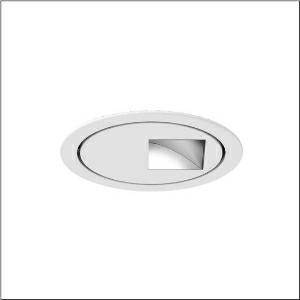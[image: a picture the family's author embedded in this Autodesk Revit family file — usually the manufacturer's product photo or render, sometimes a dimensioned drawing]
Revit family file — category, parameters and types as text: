
# Revit family: lunis_11_mini_round_51dk11cd2wm21
name_source: partatom
category: Lighting Fixtures
units: mm (PartAtom-declared; Revit-internal decimal feet)

## family parameters
Cut with Voids When Loaded = No
Host = Face
Light Source = No
Part Type = Normal
Room Calculation Point = No
Round Connector Dimension = Use Diameter
Shared = No

## types (1)
- Lunis 11 mini round (1 x LED 3000K / CRI = 90 (unbekannt), 1930 lm, 3000K)
    Apparent Load = 28 VA
    CIE Flux Codes = 44 77 97 100 100
    Color Rendering = 90
    Color Temperature = 3000K
    Default Elevation = 1800 mm
    Description = Lunis 11 mini round, downlight, light control with wallwasher, of highly reflective aluminium, highly specular, light emission: direct distribution, LED rated luminous flux: 1.930lm, light colour: 930, control gear: ECG, with terminal, 5-pole, mains connection: 220..230V, AC/DC, 0/50..60Hz, LED module, luminaire module, of aluminium, highly specular, white, diameter: 176mm, clamping range: 1..40mm, recessing ring, of plastic, traffic white (RAL 9016), protection rating (complete): IP20, insulation class (complete): insulation class II (safety insulation), certification: CE, permissible ambient temperature for indoor applications: 0..+35°C, packaging unit: 1 piece
    Height = 0 mm  [stored 0 ft]
    Lamp = 1 x LED 3000K / CRI >= 90 (unbekannt)
    Lamp Light Flux = 1930 lm
    Lamp count = 1
    Length = 176 mm
    Luminous efficacy = 69 lm/W
    Manufacturer = Siteco
    ModVariant = No
    Model = 51DK11CD2WM21
    Mounting Place = Ceiling
    Mounting Type = Recessed
    Number of Poles = 1
    OnlyDefault = Yes
    Power Factor = 1
    Product Name = Lunis 11 mini round
    Product group = downlight
    ProductGroupID = 401
    Protection Class = Protection class II
    Protection Degree = IP 20
    RLX_Detail_Level = 1
    RLX_Emergency_Light_Flux = 0 lm
    RLX_Emergency_Type = 0
    RLX_Emergency_Type_DB = No
    RlxData = <blob elided: 59305 chars, md5=25a6d3fb>
    Socket = socket
    Standby Power = 0 W
    System Light Flux = 1930 lm
    System Power = 28 W
    Type Comments = Product without accessories
    Type Image = l_1004772.jpg
    URL = http://relux.com
    VarID = ---
    Voltage = 0 V
    Weight = 0.00 kg
    Width = 176 mm

note: [stored X ft] marks values corroborated as IEEE doubles in the binary element streams (Revit-internal decimal feet)

## geometry (parser evidence)
native form markers: Blend x4, Sweep x10
no freeform markers — native parametric forms only
